# Revit family: Semi_Circular_Wash_Fountain-ADA-Acorn-3423
name_source: partatom
category: Plumbing Fixtures
units: mm (PartAtom-declared; Revit-internal decimal feet)

## family parameters
Cut with Voids When Loaded = No
Host = Face
OmniClass Number = 23.45.05.14.14
OmniClass Title = Sinks/Lavatories
Part Type = Normal
Room Calculation Point = No
Round Connector Dimension = Use Diameter
Shared = Yes

## types (1)
- 3423-ADA-1-SO-DV-VPB-MXTP
    -1 Off-Floor, Wall Outlet = Yes
    -2 On-Floor, Wall Outlet = No
    -CB Column Braced to Backsplash = No
    -DV Liquid / Lotion Soap Dispenser = Yes
    -EG Enviro-Glaze Color, Bowl and Sprayhead = No
    -H Hand Operation = No
    -HB Hose Bibb, Left Side (Not ADA Compliant) = No
    -HB Hose Bibb, Right Side (Not ADA Compliant) = No
    -JH31 31" Junior Rim Height = No
    -LBS Less Backsplash = No
    -MXTP Thermostatic/Pressure Balancing Mixing Valve = Yes
    -PCB Pipe Column Brace (Pipe By Others) = No
    -PDM Metering Liquid Soap Dispenser = No
    -PPZ Programmable Piezo Pushbutton Electronic Metering = No
    -SO Sensor Operation = Yes
    -SO-BAT Sensor Operation, Battery Powered = No
    -SPX 16 Gage Stainless Steel Housing = No
    -ST Single Temperature Valve = No
    -TM C or Multi-Fold Paper Towel Dispenser (Not ADA Compliant) = No
    -TS Single-Fold Paper Towel Dispenser (Not ADA Copliant) = No
    -VPB Vinyl Clad Enlocsure = Yes
    3423-ADA Semi-Circular, Three Station = Yes
    3424-ADA Semi-Circular, Four Station = No
    Assembly Code = D2010810
    CW Connection = Yes
    CWFU = 1.5
    Cold Water Connection Description = 1/2" NPTE CW Supply
    Cold Water Connection Diameter = 1/2"
    Current for -SO = 3 A
    Default Elevation = 0"
    Description = Three Station, ADA, Semi-Circular Wash Fountain
    Finish = Metal-Acorn-Stainless Steel-Satin
    Finish- Enclosure = Metal-Acorn-Vinyl Clad
    Finish- Sensor = Plastic-Acorn-Black
    Flow Rate = 0.5 GPM
    HW Connection = Yes
    HWFU = 1.5
    Hot Water Connection Description = 1/2" NPTE HW Supply
    Hot Water Connection Diameter = 1/2"
    Installation Instruction Link = https://www.acorneng.com
    Installation Type = Wall Mounted
    Length = 32"
    Manufacturer = Acorn Engineering
    Material = Metal-Acorn-Stainless Steel-Satin
    Maximum Water Temperature = 105° F
    Min Max. Operating Pressure = 30 PSI-100 PSI
    Model = 3423-ADA-1-SO-DV-VPB-MXTP
    Power Suply for -SO = 120 VA
    Product Documentation Link = https://www.acorneng.com
    Product Page URL = https://www.acorneng.com
    Revised Date = 09/12/2024
    URL = http://www.acorneng.com
    Vent Connection = No
    WFU = 2
    Waste Connection = Yes
    Waste Connection Diameter = 1 1/2"
    Width = 38"

## geometry (parser evidence)
native form markers: Sweep x2
no freeform markers — native parametric forms only
